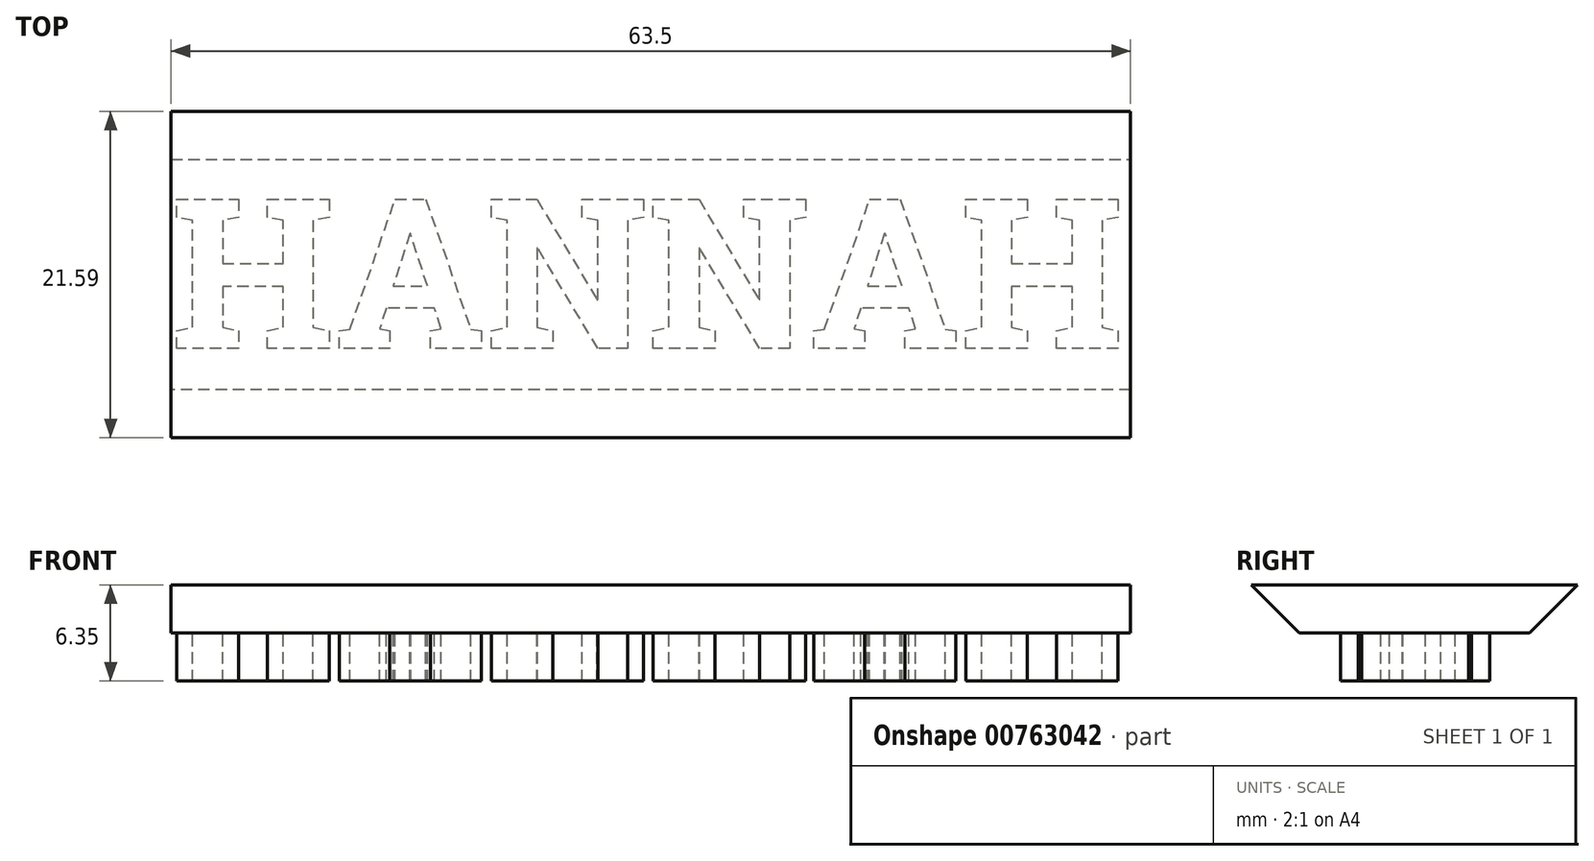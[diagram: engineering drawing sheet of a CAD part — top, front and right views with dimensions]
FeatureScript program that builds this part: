
annotation { "Feature Type Name" : "Feature", "Feature Type Description" : "" }
export const myFeature = defineFeature(function(context is Context, id is Id, definition is map)
    precondition{}
    {
        {
            var Q0;
            Q0=qCreatedBy(makeId("Top.planeOp"),FACE);
            var sketch = newSketch(context, id + "F0", { "sketchPlane" : qUnion([Q0])});
            skLineSegment(sketch, "E0.bottom", {"start": v(0, 0) * mm, "end": v(63.5, 0) * mm});
            skLineSegment(sketch, "E0.top", {"start": v(0, 25.4) * mm, "end": v(63.5, 25.4) * mm});
            skLineSegment(sketch, "E0.left", {"start": v(0, 0) * mm, "end": v(0, 25.4) * mm});
            skLineSegment(sketch, "E0.right", {"start": v(63.5, 0) * mm, "end": v(63.5, 25.4) * mm});
            skSolve(sketch);
        }
        {
            var Q0;
            Q0=makeQuery(id+"F0.imprint","IMPRINT",FACE,{"disambiguationData":[TD([[makeQuery(id+"F0.imprint","IMPRINT",EDGE,{"derivedFrom":sQuery(id+"F0.wireOp",EDGE,"E0.bottom")}),1.0]])]});
            extrude(context, id + "F1", {"entities" : qUnion([Q0]), "depth" : 3.17 * mm, "offsetDistance" : 25.4 * mm});
        }
        {
            var Q0;
            Q0=makeQuery(id+"F1.opExtrude","CAP_FACE",FACE,{"disambiguationData":[OSD([sQuery(id+"F0.wireOp",EDGE,"E0.bottom"),sQuery(id+"F0.wireOp",EDGE,"E0.top"),sQuery(id+"F0.wireOp",EDGE,"E0.left"),sQuery(id+"F0.wireOp",EDGE,"E0.right")])],"isStart":false});
            var sketch = newSketch(context, id + "F2", { "sketchPlane" : qUnion([Q0])});
            skText(sketch, "E1", { "text": "HANNAH", "fontName": "RobotoSlab-Bold.ttf"});
            const initialGuessF2  = {"E1": [0, 0.0078, 1, 0, 0.00999]};
            skSetInitialGuess(sketch, initialGuessF2);
            skSolve(sketch);
        }
        {
            var Q0;
            Q0 = qSketchRegion(id + "F2", true);
            extrude(context, id + "F3", {"entities" : qUnion([Q0]), "operationType" : NewBodyOperationType.ADD, "oppositeDirection" : true, "depth" : 6.35 * mm, "offsetDistance" : 25.4 * mm});
        }
        {
            var Q0;
            Q0=makeQuery(id+"F1.opExtrude","CAP_EDGE",EDGE,{"disambiguationData":[OSD([sQuery(id+"F0.wireOp",EDGE,"E0.top")])],"isStart":true});
            chamfer(context, id + "F4", {"entities" : qUnion([Q0]), "width" : 5.08 * mm, "tangentPropagation" : true});
        }
        {
            var Q0;
            Q0=makeQuery(id+"F1.opExtrude","CAP_EDGE",EDGE,{"disambiguationData":[OSD([sQuery(id+"F0.wireOp",EDGE,"E0.bottom")])],"isStart":true});
            chamfer(context, id + "F5", {"entities" : qUnion([Q0]), "width" : 5.08 * mm, "tangentPropagation" : true});
        }
    });
